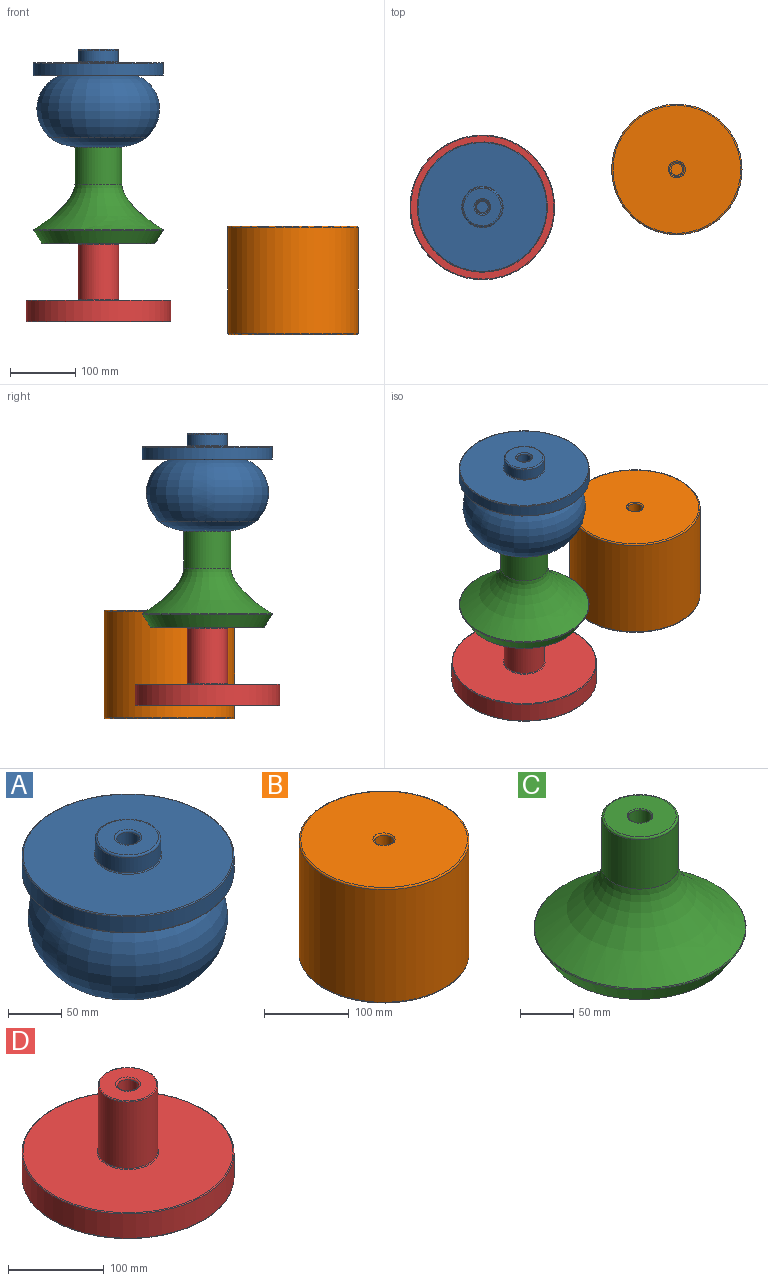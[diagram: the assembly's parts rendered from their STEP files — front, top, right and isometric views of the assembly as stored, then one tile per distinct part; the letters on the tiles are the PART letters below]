
ASSEMBLY  parts=4 mates=4
PART A: 19 faces, bbox 216x216x165 mm
  f0: plane 17.6x17.6mm, normal (0,0,-1), area 243.3mm2, adj f18
  f1: plane 17.6x17.6mm, normal (0,0,1), area 243.3mm2, adj f2
  f2: torus R=8.8mm, axis (0,0,-1), area 198.8mm2, adj f1,f3
  f3: cylinder r=10.8mm len=26mm, axis (0,0,-1), area 1764.3mm2, adj f2,f4
  f4: torus R=12.8mm, axis (0,0,-1), area 227.5mm2, adj f3,f5
  f5: plane 57.6x57.6mm, normal (0,0,1), area 2091mm2, adj f4,f6
  f6: torus R=28.8mm, axis (0,0,-1), area 593.6mm2, adj f5,f7
  f7: cylinder r=30.8mm len=61.6mm, axis (0,0,-1), area 3333.7mm2, adj f6,f8
  f8: torus R=31.8mm, axis (0,0,-1), area 307.6mm2, adj f7,f9
  f9: plane 197.6x197.6mm, normal (0,0,1), area 27489.6mm2, adj f8,f10
  f10: torus R=98.8mm, axis (0,0,-1), area 981.4mm2, adj f9,f11
  f11: cylinder r=99.8mm len=199.6mm, axis (0,0,-1), area 11287.1mm2, adj f10,f12
  f12: torus R=98.8mm, axis (0,0,-1), area 981.4mm2, adj f11,f13
  f13: plane 197.6x197.6mm, normal (0,0,-1), area 19911.4mm2, adj f12,f14
  f14: revolved ~188.39x188.39mm, area 61212.5mm2, adj f13,f15
  f15: revolved ~149.19x149.19mm, area 18306.3mm2, adj f14,f16
  f16: torus R=12.8mm, axis (0,0,-1), area 225mm2, adj f15,f17
  f17: cylinder r=10.8mm len=21.6mm, axis (0,0,-1), area 748.6mm2, adj f16,f18
  f18: torus R=8.8mm, axis (0,0,-1), area 198.8mm2, adj f0,f17
PART B: 9 faces, bbox 216.5x216.5x166.1 mm
  f0: torus R=9mm, axis (0,0,1), area 202.8mm2, adj f1,f8
  f1: cylinder r=11mm len=26mm, axis (0,0,1), area 1797mm2, adj f0,f2
  f2: torus R=13mm, axis (0,0,1), area 231.5mm2, adj f1,f3
  f3: plane 196x196mm, normal (0,0,1), area 29640.9mm2, adj f2,f4
  f4: torus R=98mm, axis (0,0,1), area 1959.6mm2, adj f3,f5
  f5: cylinder r=100mm len=200mm, axis (0,0,1), area 101835mm2, adj f4,f6
  f6: torus R=98mm, axis (0,0,1), area 1959.6mm2, adj f5,f7
  f7: plane 196x196mm, normal (0,0,-1), area 30171.9mm2, adj f6
  f8: plane 18x18mm, normal (0,0,1), area 254.5mm2, adj f0
PART C: 16 faces, bbox 215.6x215.6x165 mm
  f0: plane 20x20mm, normal (0,0,1), area 314.2mm2, adj f1
  f1: torus R=10mm, axis (0,0,1), area 105mm2, adj f0,f2
  f2: cylinder r=11mm len=28mm, axis (0,0,1), area 1935.2mm2, adj f1,f3
  f3: torus R=12mm, axis (0,0,1), area 112.2mm2, adj f2,f4
  f4: plane 68x68mm, normal (0,0,1), area 3179.3mm2, adj f3,f5
  f5: torus R=34mm, axis (0,0,1), area 696.3mm2, adj f4,f6
  f6: cylinder r=36mm len=72mm, axis (0,0,1), area 12841.8mm2, adj f5,f7
  f7: revolved ~198.2x198.2mm, area 38020mm2, adj f6,f8
  f8: torus R=98.6mm, axis (0,0,1), area 1004.8mm2, adj f7,f9
  f9: cone r=99.44mm half-angle=32.3deg, axis (0,0,1), area 13706.5mm2, adj f8,f10
  f10: torus R=86.09mm, axis (0,0,1), area 547.7mm2, adj f9,f11
  f11: plane 172.18x172.18mm, normal (0,0,-1), area 22770mm2, adj f10,f12
  f12: torus R=12.8mm, axis (0,0,1), area 227.5mm2, adj f11,f13
  f13: cylinder r=10.8mm len=21.6mm, axis (0,0,1), area 746.4mm2, adj f12,f14
  f14: torus R=8.8mm, axis (0,0,1), area 198.8mm2, adj f13,f15
  f15: plane 17.6x17.6mm, normal (0,0,-1), area 243.3mm2, adj f14
PART D: 13 faces, bbox 240.3x240.3x120 mm
  f0: torus R=13mm, axis (0,0,-1), area 231.5mm2, adj f1,f12
  f1: plane 60x60mm, normal (0,0,1), area 2296.5mm2, adj f0,f2
  f2: torus R=30mm, axis (0,0,-1), area 302.4mm2, adj f1,f3
  f3: cylinder r=31mm len=85mm, axis (0,0,-1), area 16556.2mm2, adj f2,f4
  f4: torus R=32mm, axis (0,0,-1), area 309.5mm2, adj f3,f5
  f5: plane 220x220mm, normal (0,0,1), area 34796.3mm2, adj f4,f6
  f6: torus R=110mm, axis (0,0,-1), area 1091.9mm2, adj f5,f7
  f7: cylinder r=111mm len=222mm, axis (0,0,-1), area 21620.4mm2, adj f6,f8
  f8: torus R=110mm, axis (0,0,-1), area 1091.9mm2, adj f7,f9
  f9: plane 220x220mm, normal (0,0,-1), area 38013.3mm2, adj f8
  f10: plane 16x16mm, normal (0,0,1), area 201.1mm2, adj f11
  f11: torus R=8mm, axis (0,0,-1), area 293.4mm2, adj f10,f12
  f12: cylinder r=11mm len=25mm, axis (0,0,-1), area 1727.9mm2, adj f0,f11
PLACE A t=(-154.44,-35.38,71.66)mm
PLACE B t=(154.79,22.8,-190.31)mm
PLACE C t=(-143.64,-35.38,-70.81)mm
PLACE D t=(-143.64,-35.38,-231.01)mm
MATE parallel C.f1 <-> A.f2  axis (0,0,1) through (-143.64,-35.38,-24.17)mm
MATE parallel B.f0 <-> C.f1  axis (0,0,1) through (154.79,22.8,-117.59)mm
MATE parallel B.f0 <-> C.f1  axis (0,0,1) through (154.79,22.8,-147.59)mm
MATE parallel D.f0 <-> A.f2  axis (0,0,1) through (-143.64,-35.38,-174.01)mm
